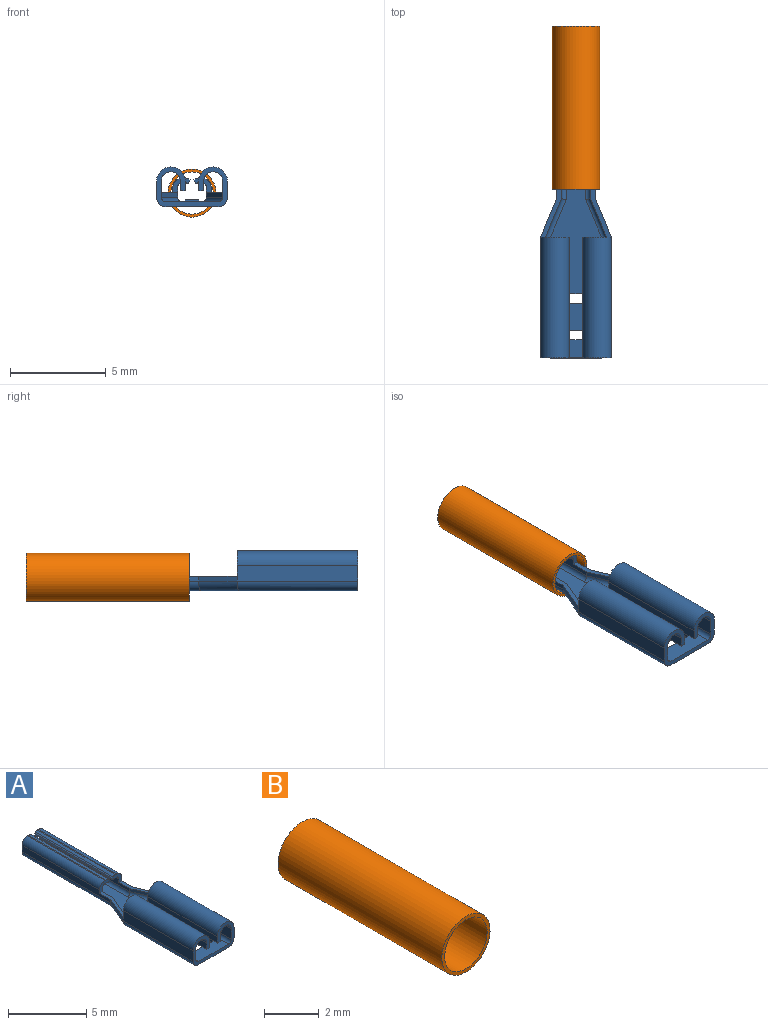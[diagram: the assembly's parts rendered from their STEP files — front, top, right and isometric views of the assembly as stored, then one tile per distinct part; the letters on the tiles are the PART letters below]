
ASSEMBLY  parts=2 mates=1
PART A: 76 faces, bbox 3.7x16.3x2.1 mm
  f0: plane 3x1.1mm, normal (0,0,1), area 0.8mm2, adj f1,f39,f40,f41,f42,f65
  f1: plane 1.5x1.32mm, normal (0,1,0), area 0.8mm2, adj f0,f14,f15,f16,f17,f18,f19,f20
  f2: plane 16.3x2.7mm, normal (0,0,1), area 25.4mm2, adj f3,f21,f22,f23,f25,f26,f27,f28
  f3: plane 2x0.35mm, normal (0,1,0), area 0.5mm2, adj f2,f4,f25,f27,f32,f33,f34,f35
  f4: plane 16.3x2.7mm, normal (0,0,-1), area 25.6mm2, adj f3,f12,f13,f23,f25,f26,f27,f28
  f5: plane 6.3x0.82mm, normal (1,0,0), area 5.2mm2, adj f6,f22,f23,f24,f43
  f6: cylinder r=0.5mm len=6.3mm, axis (0,1,0), area 9.9mm2, adj f5,f7,f23,f24
  f7: plane 6.3x0.49mm, normal (-1,0,0), area 3.1mm2, adj f6,f8,f23,f24
  f8: plane 6.3x0.25mm, normal (0,0,-1), area 1.6mm2, adj f7,f9,f23,f24
  f9: plane 6.3x0.49mm, normal (1,0,0), area 3.1mm2, adj f8,f10,f23,f24
  f10: cylinder r=0.75mm len=6.3mm, axis (0,1,0), area 14.8mm2, adj f9,f11,f23,f24
  f11: plane 6.3x0.82mm, normal (-1,0,0), area 5.2mm2, adj f10,f12,f23,f24,f44
  f12: cylinder r=0.5mm len=6.3mm, axis (0,1,0), area 4.9mm2, adj f4,f11,f23,f48
  f13: cylinder r=0.5mm len=6.3mm, axis (0,1,0), area 4.9mm2, adj f4,f14,f23,f50
  f14: plane 6.3x0.82mm, normal (1,0,0), area 5.2mm2, adj f1,f13,f15,f23,f42
  f15: cylinder r=0.75mm len=6.3mm, axis (0,1,0), area 14.8mm2, adj f1,f14,f16,f23
  f16: plane 6.3x0.49mm, normal (-1,0,0), area 3.1mm2, adj f1,f15,f17,f23
  f17: plane 6.3x0.25mm, normal (0,0,-1), area 1.6mm2, adj f1,f16,f18,f23
  f18: plane 6.3x0.49mm, normal (1,0,0), area 3.1mm2, adj f1,f17,f19,f23
  f19: cylinder r=0.5mm len=6.3mm, axis (0,1,0), area 9.9mm2, adj f1,f18,f20,f23
  f20: plane 6.3x0.82mm, normal (-1,0,0), area 5.2mm2, adj f1,f19,f21,f23,f39
  f21: cylinder r=0.25mm len=6.3mm, axis (0,1,0), area 2.5mm2, adj f2,f20,f23,f53
  f22: cylinder r=0.25mm len=6.3mm, axis (0,1,0), area 2.5mm2, adj f2,f5,f23,f55
  f23: plane 3.7x2.07mm, normal (0,-1,0), area 2.6mm2, adj f2,f4,f5,f6,f7,f8,f9,f10
  f24: plane 1.5x1.32mm, normal (0,1,0), area 0.8mm2, adj f5,f6,f7,f8,f9,f10,f11,f47
  f25: plane 0.5x0.25mm, normal (1,0,0), area 0.1mm2, adj f2,f3,f4,f26
  f26: plane 2x0.25mm, normal (0,-1,0), area 0.5mm2, adj f2,f4,f25,f27
  f27: plane 0.5x0.25mm, normal (-1,0,0), area 0.1mm2, adj f2,f3,f4,f26
  f28: plane 2x0.25mm, normal (0,1,0), area 0.5mm2, adj f2,f4,f29,f31
  f29: plane 0.5x0.25mm, normal (1,0,0), area 0.1mm2, adj f2,f4,f28,f30
  f30: plane 2x0.35mm, normal (0,-1,0), area 0.5mm2, adj f2,f4,f29,f31,f32,f33,f34,f35
  f31: plane 0.5x0.25mm, normal (-1,0,0), area 0.1mm2, adj f2,f4,f28,f30
  f32: plane 1.4x0.5mm, normal (0,0,-1), area 0.7mm2, adj f3,f30,f36,f37
  f33: plane 1.4x0.7mm, normal (0,0,1), area 1mm2, adj f3,f30,f34,f35
  f34: plane 1.4x0.1mm, normal (-0.71,0,0.71), area 0.2mm2, adj f2,f3,f30,f33
  f35: plane 1.4x0.1mm, normal (0.71,0,0.71), area 0.2mm2, adj f2,f3,f30,f33
  f36: plane 1.4x0.1mm, normal (0.71,0,-0.71), area 0.2mm2, adj f3,f4,f30,f32
  f37: plane 1.4x0.1mm, normal (-0.71,0,-0.71), area 0.2mm2, adj f3,f4,f30,f32
  f38: plane 2x1.5mm, normal (0,1,0), area 1.3mm2, adj f2,f4,f40,f41,f45,f46,f49,f51
  f39: plane 2x0.85mm, normal (-0.92,-0.39,0), area 0.5mm2, adj f0,f20,f40,f53
  f40: plane 8x0.5mm, normal (-1,0,0), area 3.8mm2, adj f0,f38,f39,f52,f61,f65
  f41: plane 8x0.5mm, normal (1,0,0), area 3.8mm2, adj f0,f38,f42,f51,f60,f65
  f42: plane 2x0.85mm, normal (0.92,0.39,0), area 0.5mm2, adj f0,f14,f41,f50
  f43: plane 2x0.85mm, normal (0.92,-0.39,0), area 0.5mm2, adj f5,f46,f47,f55
  f44: plane 2x0.85mm, normal (-0.92,0.39,0), area 0.5mm2, adj f11,f45,f47,f48
  f45: plane 8x0.5mm, normal (-1,0,0), area 3.8mm2, adj f38,f44,f47,f49,f72,f75
  f46: plane 8x0.5mm, normal (1,0,0), area 3.8mm2, adj f38,f43,f47,f54,f71,f75
  f47: plane 3x1.1mm, normal (0,0,1), area 0.8mm2, adj f24,f43,f44,f45,f46,f75
  f48: cylinder r=0.5mm len=2.29mm, axis (0.39,0.92,0), area 1.7mm2, adj f4,f12,f44,f49
  f49: cylinder r=0.5mm len=8.1mm, axis (0,1,0), area 6.3mm2, adj f4,f38,f45,f48
  f50: cylinder r=0.5mm len=2.29mm, axis (0.39,-0.92,0), area 1.7mm2, adj f4,f13,f42,f51
  f51: cylinder r=0.5mm len=8.1mm, axis (0,-1,0), area 6.3mm2, adj f4,f38,f41,f50
  f52: cylinder r=0.25mm len=8.05mm, axis (0,-1,0), area 3.1mm2, adj f2,f38,f40,f53
  f53: cylinder r=0.25mm len=2.14mm, axis (0.39,-0.92,0), area 0.9mm2, adj f2,f21,f39,f52
  f54: cylinder r=0.25mm len=8.05mm, axis (0,1,0), area 3.1mm2, adj f2,f38,f46,f55
  f55: cylinder r=0.25mm len=2.14mm, axis (0.39,0.92,0), area 0.9mm2, adj f2,f22,f43,f54
  f56: plane 7x0.2mm, normal (-0.89,0,-0.45), area 1.6mm2, adj f38,f57,f64,f65
  f57: plane 7x0.1mm, normal (-0.45,0,0.89), area 0.8mm2, adj f38,f56,f58,f65
  f58: cylinder r=0.5mm len=7mm, axis (0,1,0), area 1.6mm2, adj f38,f57,f59,f65
  f59: plane 7x0.08mm, normal (0,0,1), area 0.6mm2, adj f38,f58,f60,f65
  f60: cylinder r=0.5mm len=7mm, axis (0,1,0), area 5.5mm2, adj f38,f41,f59,f65
  f61: cylinder r=0.25mm len=7mm, axis (0,1,0), area 2.7mm2, adj f38,f40,f62,f65
  f62: plane 7x0.14mm, normal (0,0,-1), area 1mm2, adj f38,f61,f63,f65
  f63: cylinder r=0.25mm len=7mm, axis (0,1,0), area 0.8mm2, adj f38,f62,f64,f65
  f64: plane 7x0.05mm, normal (0.45,0,-0.89), area 0.4mm2, adj f38,f56,f63,f65
  f65: plane 0.9x0.75mm, normal (0,-1,0), area 0.3mm2, adj f0,f40,f41,f56,f57,f58,f59,f60
  f66: plane 7x0.1mm, normal (0.45,0,0.89), area 0.8mm2, adj f38,f67,f74,f75
  f67: plane 7x0.2mm, normal (0.89,0,-0.45), area 1.6mm2, adj f38,f66,f68,f75
  f68: plane 7x0.05mm, normal (-0.45,0,-0.89), area 0.4mm2, adj f38,f67,f69,f75
  f69: cylinder r=0.25mm len=7mm, axis (0,1,0), area 0.8mm2, adj f38,f68,f70,f75
  f70: plane 7x0.14mm, normal (0,0,-1), area 1mm2, adj f38,f69,f71,f75
  f71: cylinder r=0.25mm len=7mm, axis (0,1,0), area 2.7mm2, adj f38,f46,f70,f75
  f72: cylinder r=0.5mm len=7mm, axis (0,1,0), area 5.5mm2, adj f38,f45,f73,f75
  f73: plane 7x0.08mm, normal (0,0,1), area 0.6mm2, adj f38,f72,f74,f75
  f74: cylinder r=0.5mm len=7mm, axis (0,1,0), area 1.6mm2, adj f38,f66,f73,f75
  f75: plane 0.9x0.75mm, normal (0,-1,0), area 0.3mm2, adj f45,f46,f47,f66,f67,f68,f69,f70
PART B: 4 faces, bbox 2.5x8.5x2.5 mm
  f0: cylinder r=1.1mm len=8.5mm, axis (0,1,0), area 58.7mm2, adj f2,f3
  f1: cylinder r=1.25mm len=8.5mm, axis (0,1,0), area 66.8mm2, adj f2,f3
  f2: plane 2.5x2.5mm, normal (0,-1,0), area 1.1mm2, adj f0,f1
  f3: plane 2.5x2.5mm, normal (0,1,0), area 1.1mm2, adj f0,f1
PLACE A t=(-3.19,-3.05,2)mm
PLACE B t=(-3.19,-3.05,1.97)mm
MATE fastened A.f38 <-> B.f0  axis (0,1,0) through (-3.19,6.95,1.68)mm
